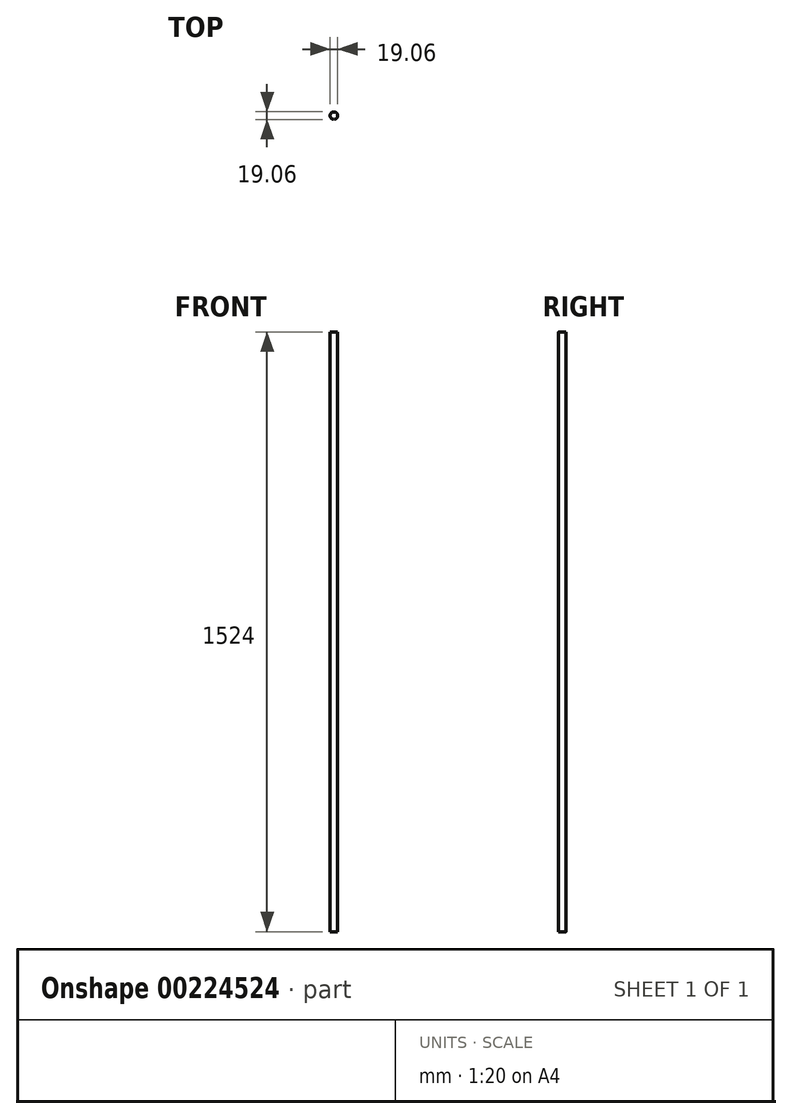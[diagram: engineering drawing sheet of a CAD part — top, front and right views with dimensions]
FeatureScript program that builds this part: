
annotation { "Feature Type Name" : "Feature", "Feature Type Description" : "" }
export const myFeature = defineFeature(function(context is Context, id is Id, definition is map)
    precondition{}
    {
        {
            var Q0;
            Q0=qCreatedBy(makeId("Top.planeOp"),FACE);
            var sketch = newSketch(context, id + "F0", { "sketchPlane" : qUnion([Q0])});
            skCircle(sketch, "E0", {"center": v(0, 0) * mm, "radius": 9.53 * mm});
            skSolve(sketch);
        }
        {
            var Q0;
            Q0 = qSketchRegion(id + "F0", true);
            extrude(context, id + "F1", {"entities" : qUnion([Q0]), "oppositeDirection" : true, "depth" : 1524 * mm});
        }
    });
